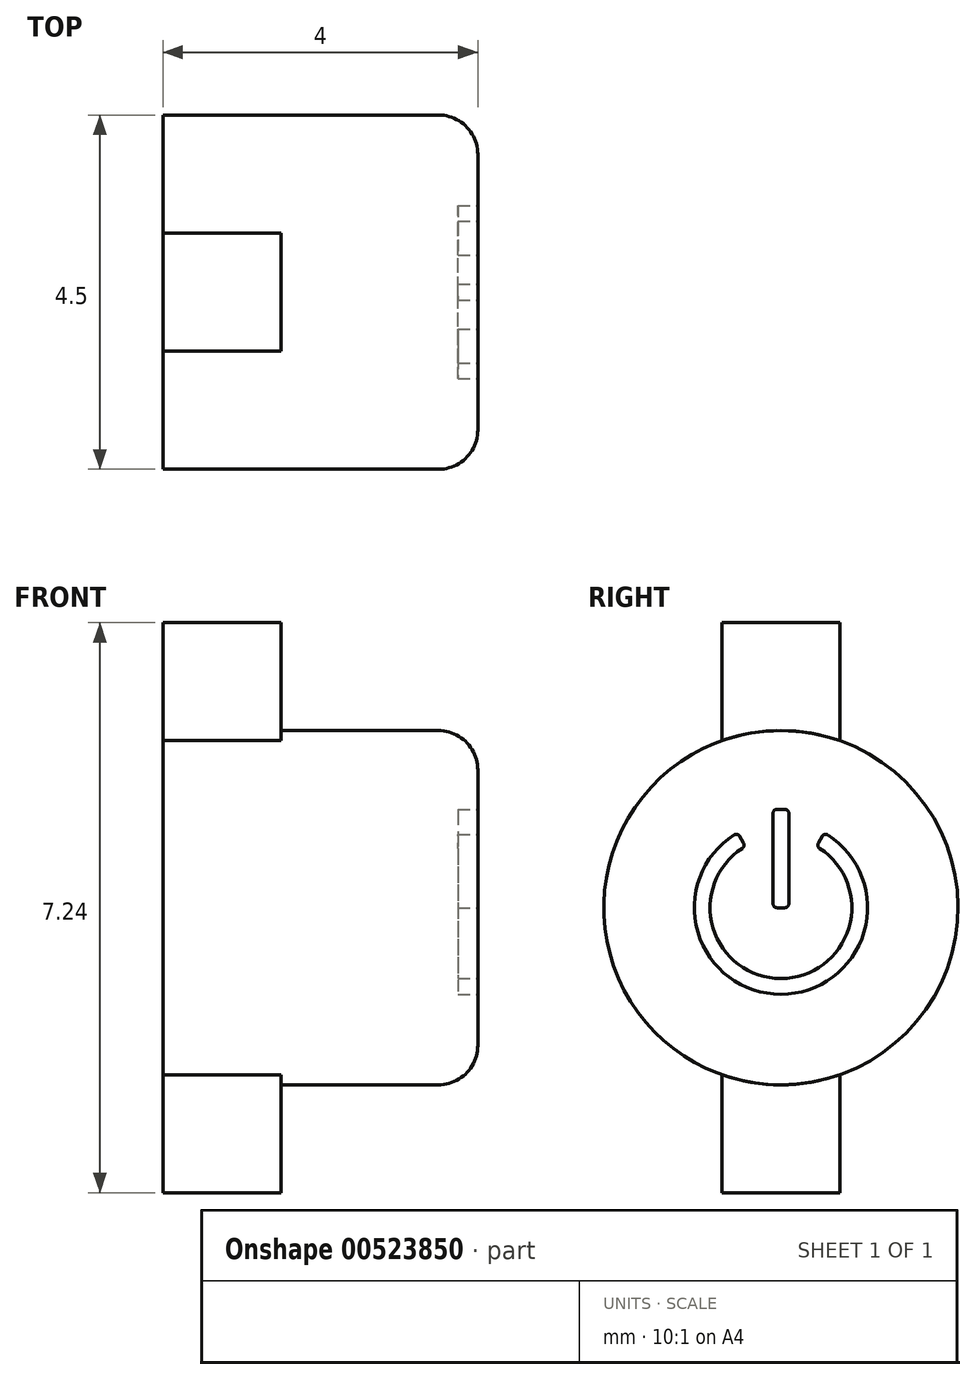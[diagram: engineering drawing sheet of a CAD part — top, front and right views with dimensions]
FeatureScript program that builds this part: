
annotation { "Feature Type Name" : "Feature", "Feature Type Description" : "" }
export const myFeature = defineFeature(function(context is Context, id is Id, definition is map)
    precondition{}
    {
        {
            var Q0;
            Q0=qCreatedBy(makeId("Right.planeOp"),FACE);
            var sketch = newSketch(context, id + "F0", { "sketchPlane" : qUnion([Q0])});
            skCircle(sketch, "E0", {"center": v(0, 0) * mm, "radius": 2.25 * mm});
            skSolve(sketch);
        }
        {
            var Q0;
            Q0=makeQuery(id+"F0.imprint","IMPRINT",FACE,{"disambiguationData":[TD([[makeQuery(id+"F0.imprint","IMPRINT",EDGE,{"derivedFrom":sQuery(id+"F0.wireOp",EDGE,"E0")}),1.0]])]});
            extrude(context, id + "F1", {"entities" : qUnion([Q0]), "endBound" : BoundingType.SYMMETRIC, "depth" : 4 * mm, "offsetDistance" : 25 * mm});
        }
        {
            var Q0;
            Q0=makeQuery(id+"F1.opExtrude","CAP_FACE",FACE,{"disambiguationData":[OSD([sQuery(id+"F0.wireOp",EDGE,"E0")])],"isStart":false});
            fillet(context, id + "F2", {"entities" : qUnion([Q0]), "radius" : 0.5 * mm, "tangentPropagation" : true, "allowEdgeOverflow" : false});
        }
        {
            var Q0;
            Q0=makeQuery(id+"F1.opExtrude","CAP_FACE",FACE,{"disambiguationData":[OSD([sQuery(id+"F0.wireOp",EDGE,"E0")])],"isStart":true});
            var sketch = newSketch(context, id + "F3", { "sketchPlane" : qUnion([Q0])});
            skArc(sketch, "E1", {"start": v(-0.77, -2.11) * mm, "mid": v(2.25, -0.01) * mm, "end": v(-0.75, 2.12) * mm});
            skLineSegment(sketch, "E2.top", {"start": v(-0.75, 3.62) * mm, "end": v(0.75, 3.62) * mm});
            skLineSegment(sketch, "E2.left", {"start": v(-0.75, 2.12) * mm, "end": v(-0.75, 3.62) * mm});
            skLineSegment(sketch, "E2.right", {"start": v(0.75, 2.12) * mm, "end": v(0.75, 3.62) * mm});
            skPoint(sketch, "E2.middle", {"position": v(0, 3.06) * mm});
            skPoint(sketch, "E3.orphan", {"position": v(-0.75, 2.5) * mm});
            skPoint(sketch, "E4.orphan", {"position": v(0.75, 2.5) * mm});
            skLineSegment(sketch, "E5.MirrorCS", {"start": v(0.75, -2.12) * mm, "end": v(0.75, -3.62) * mm});
            skLineSegment(sketch, "E6.MirrorCS", {"start": v(-0.75, -2.12) * mm, "end": v(-0.75, -3.62) * mm});
            skLineSegment(sketch, "E7.MirrorCS", {"start": v(-0.75, -3.62) * mm, "end": v(0.75, -3.62) * mm});
            skPoint(sketch, "E8.MirrorP", {"position": v(-0.75, -2.5) * mm});
            skPoint(sketch, "E9.MirrorP", {"position": v(0, -3.06) * mm});
            skPoint(sketch, "E10.MirrorP", {"position": v(0.75, -2.5) * mm});
            skSolve(sketch);
        }
        {
            var Q0;
            Q0=qSketchRegion(id+"F3",true);
            extrude(context, id + "F4", {"entities" : qUnion([Q0]), "operationType" : NewBodyOperationType.ADD, "oppositeDirection" : true, "depth" : 1.5 * mm, "offsetDistance" : 25 * mm});
        }
        {
            var Q0;
            Q0=makeQuery(id+"F1.opExtrude","CAP_FACE",FACE,{"disambiguationData":[OSD([sQuery(id+"F0.wireOp",EDGE,"E0")])],"isStart":false});
            var sketch = newSketch(context, id + "F5", { "sketchPlane" : qUnion([Q0])});
            skLineSegment(sketch, "E11.bottom", {"start": v(-0.05, 1.25) * mm, "end": v(0.05, 1.25) * mm});
            skLineSegment(sketch, "E11.left", {"start": v(-0.1, 1.2) * mm, "end": v(-0.1, 0.05) * mm});
            skLineSegment(sketch, "E11.right", {"start": v(0.1, 1.2) * mm, "end": v(0.1, 0.05) * mm});
            skPoint(sketch, "E11.middle", {"position": v(0, 0) * mm});
            skLineSegment(sketch, "E12", {"start": v(-0.05, 0) * mm, "end": v(0.05, 0) * mm});
            skPoint(sketch, "E13.orphan", {"position": v(-0.1, -1.25) * mm});
            skPoint(sketch, "E14.orphan", {"position": v(0.1, -1.25) * mm});
            skArc(sketch, "E15.0", {"start": v(-0.5, 0.75) * mm, "mid": v(0, -0.9) * mm, "end": v(0.5, 0.75) * mm});
            skArc(sketch, "E16.0", {"start": v(-0.6, 0.93) * mm, "mid": v(0, -1.1) * mm, "end": v(0.6, 0.93) * mm});
            skLineSegment(sketch, "E17", {"start": v(-0.52, 0.9) * mm, "end": v(-0.47, 0.82) * mm});
            skLineSegment(sketch, "E18.trimOffspring", {"start": v(0.47, 0.82) * mm, "end": v(0.52, 0.9) * mm});
            skPoint(sketch, "E19.visualSharp", {"position": v(-0.1, 1.25) * mm});
            skArc(sketch, "E19.filletArc", {"start": v(-0.05, 1.25) * mm, "mid": v(-0.09, 1.24) * mm, "end": v(-0.1, 1.2) * mm});
            skPoint(sketch, "E20.visualSharp", {"position": v(0.1, 1.25) * mm});
            skArc(sketch, "E20.filletArc", {"start": v(0.1, 1.2) * mm, "mid": v(0.09, 1.24) * mm, "end": v(0.05, 1.25) * mm});
            skPoint(sketch, "E21.visualSharp", {"position": v(-0.1, 0) * mm});
            skArc(sketch, "E21.filletArc", {"start": v(-0.1, 0.05) * mm, "mid": v(-0.09, 0.01) * mm, "end": v(-0.05, 0) * mm});
            skPoint(sketch, "E22.visualSharp", {"position": v(0.1, 0) * mm});
            skArc(sketch, "E22.filletArc", {"start": v(0.05, 0) * mm, "mid": v(0.09, 0.01) * mm, "end": v(0.1, 0.05) * mm});
            skPoint(sketch, "E23.visualSharp", {"position": v(-0.45, 0.78) * mm});
            skArc(sketch, "E23.filletArc", {"start": v(-0.5, 0.75) * mm, "mid": v(-0.47, 0.78) * mm, "end": v(-0.47, 0.82) * mm});
            skPoint(sketch, "E24.visualSharp", {"position": v(-0.55, 0.95) * mm});
            skArc(sketch, "E24.filletArc", {"start": v(-0.52, 0.9) * mm, "mid": v(-0.56, 0.93) * mm, "end": v(-0.6, 0.93) * mm});
            skPoint(sketch, "E25.visualSharp", {"position": v(0.45, 0.78) * mm});
            skArc(sketch, "E25.filletArc", {"start": v(0.47, 0.82) * mm, "mid": v(0.47, 0.78) * mm, "end": v(0.5, 0.75) * mm});
            skPoint(sketch, "E26.visualSharp", {"position": v(0.55, 0.95) * mm});
            skArc(sketch, "E26.filletArc", {"start": v(0.6, 0.93) * mm, "mid": v(0.56, 0.93) * mm, "end": v(0.52, 0.9) * mm});
            skSolve(sketch);
        }
        {
            var Q0;
            Q0 = qSketchRegion(id + "F5", true);
            extrude(context, id + "F6", {"entities" : qUnion([Q0]), "operationType" : NewBodyOperationType.REMOVE, "oppositeDirection" : true, "depth" : .25 * mm, "offsetDistance" : 25 * mm});
        }
    });
